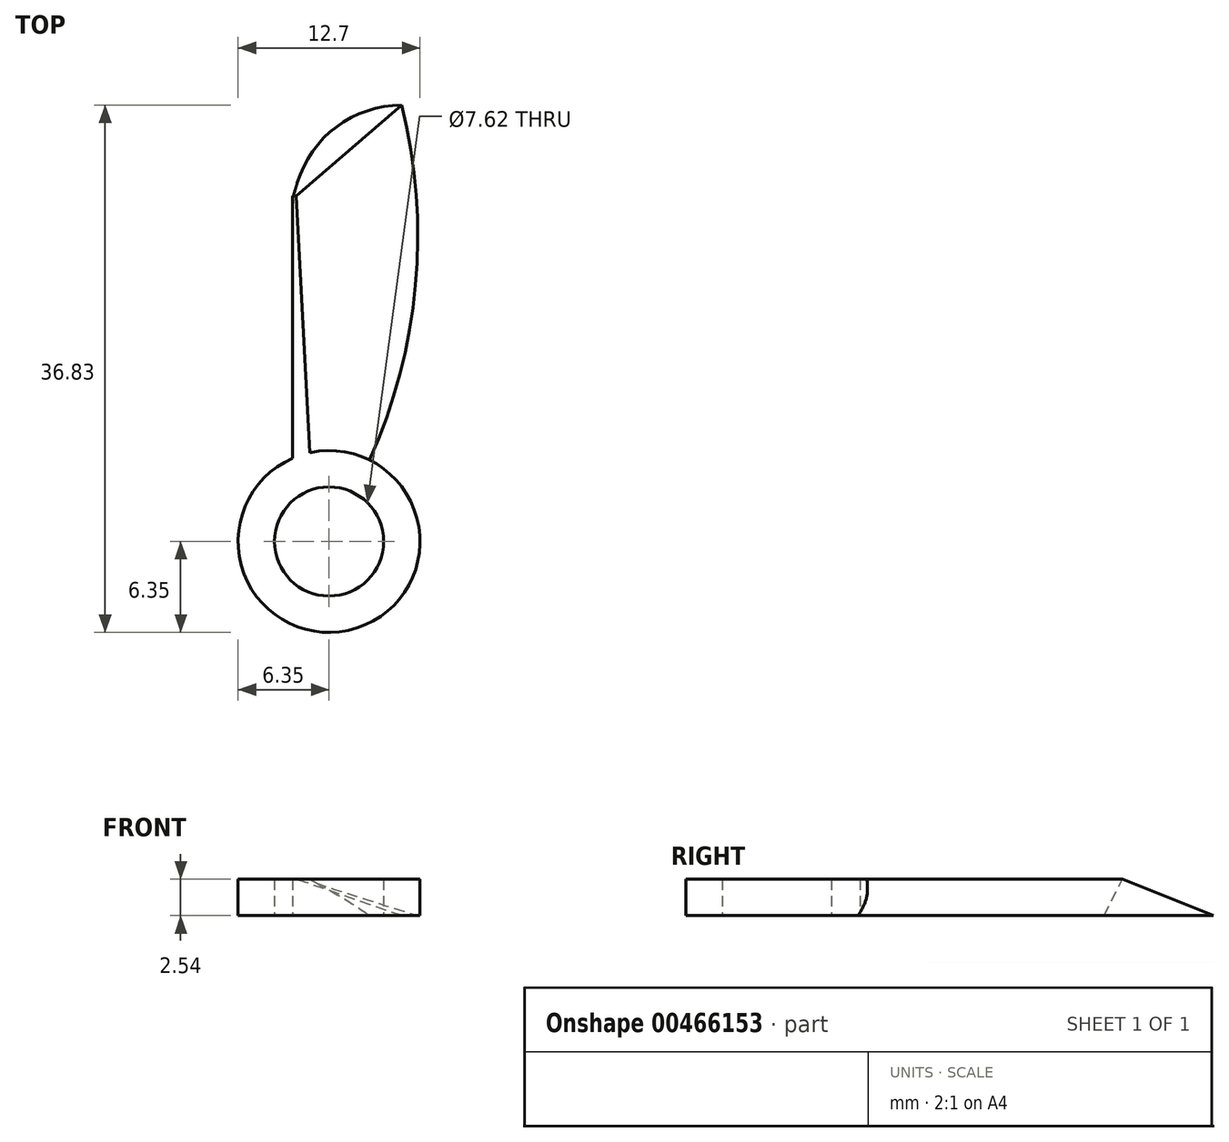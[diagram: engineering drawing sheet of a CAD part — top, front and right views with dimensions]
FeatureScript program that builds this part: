
annotation { "Feature Type Name" : "Feature", "Feature Type Description" : "" }
export const myFeature = defineFeature(function(context is Context, id is Id, definition is map)
    precondition{}
    {
        {
            var Q0;
            Q0=qCreatedBy(makeId("Top.planeOp"),FACE);
            var sketch = newSketch(context, id + "F0", { "sketchPlane" : qUnion([Q0])});
            skLineSegment(sketch, "E0", {"start": v(0, 0) * mm, "end": v(0, 17.78) * mm});
            skArc(sketch, "E1", {"start": v(7.62, 25.4) * mm, "mid": v(2.23, 23.17) * mm, "end": v(0, 17.78) * mm});
            skLineSegment(sketch, "E2", {"start": v(7.62, 17.78) * mm, "end": v(7.62, 25.4) * mm, "construction": true});
            skLineSegment(sketch, "E3", {"start": v(0, 0) * mm, "end": v(5.08, 0) * mm});
            skArc(sketch, "E4", {"start": v(5.08, 0) * mm, "mid": v(8.54, 12.48) * mm, "end": v(7.62, 25.4) * mm});
            skSolve(sketch);
        }
        {
            var Q0;
            Q0=qCreatedBy(makeId("Top.planeOp"),FACE);
            cPlane(context, id + "F1", {"entities" : qUnion([Q0]), "cplaneType" : CPlaneType.OFFSET, "offset" : 2.54 * mm, "width" : 152.4 * mm, "height" : 152.4 * mm});
        }
        {
            var Q0;
            Q0=qCreatedBy(id+"F1.planeOp",FACE);
            var sketch = newSketch(context, id + "F2", { "sketchPlane" : qUnion([Q0])});
            skLineSegment(sketch, "E5.bottom", {"start": v(0, 0) * mm, "end": v(1.27, 0) * mm});
            skLineSegment(sketch, "E5.left", {"start": v(0, 0) * mm, "end": v(0, 19.05) * mm});
            skLineSegment(sketch, "E6", {"start": v(0, 19.05) * mm, "end": v(0.25, 19.05) * mm});
            skLineSegment(sketch, "E7", {"start": v(0.25, 19.05) * mm, "end": v(1.27, 0) * mm});
            skSolve(sketch);
        }
        {
            var Q0;
            Q0 = qSketchRegion(id + "F0", true);
            var Q1;
            Q1 = qSketchRegion(id + "F2", true);
            loft(context, id + "F3", {"sheetProfilesArray" : [{ "sheetProfileEntities" : qUnion([Q0]) }, { "sheetProfileEntities" : qUnion([Q1]) }]});
        }
        {
            var Q0;
            Q0=qCreatedBy(makeId("Top.planeOp"),FACE);
            var sketch = newSketch(context, id + "F4", { "sketchPlane" : qUnion([Q0])});
            skCircle(sketch, "E8", {"center": v(2.54, -5.08) * mm, "radius": 6.35 * mm});
            skLineSegment(sketch, "E9", {"start": v(2.54, 0) * mm, "end": v(2.54, -5.08) * mm, "construction": true});
            skCircle(sketch, "E10", {"center": v(2.54, -5.08) * mm, "radius": 3.81 * mm});
            skSolve(sketch);
        }
        {
            var Q0;
            Q0 = qSketchRegion(id + "F4", true);
            var Q1;
            Q1=makeQuery(id+"F3.opLoft","CAP_FACE",FACE,{"disambiguationData":[OSD([makeQuery(id+"F2.imprint","IMPRINT",FACE,{"disambiguationData":[TD([[makeQuery(id+"F2.imprint","IMPRINT",EDGE,{"derivedFrom":sQuery(id+"F2.wireOp",EDGE,"E5.bottom")}),1.0]])]})])],"isStart":true});
            extrude(context, id + "F5", {"entities" : qUnion([Q0]), "operationType" : NewBodyOperationType.ADD, "endBound" : BoundingType.UP_TO_SURFACE, "endBoundEntityFace" : qUnion([Q1]), "depth" : 25.4 * mm});
        }
    });
